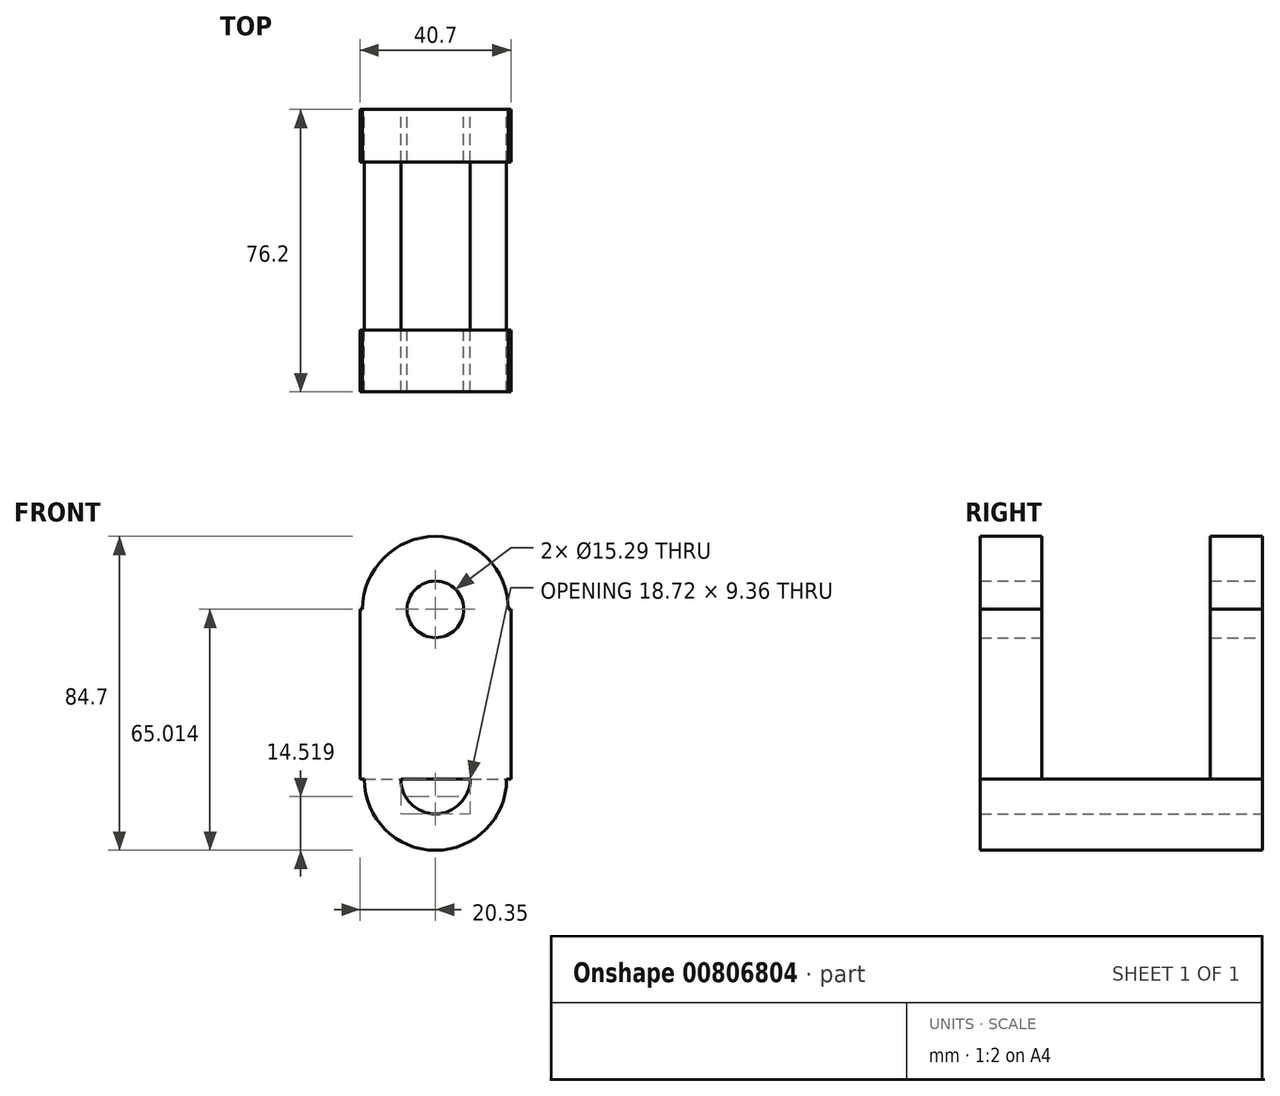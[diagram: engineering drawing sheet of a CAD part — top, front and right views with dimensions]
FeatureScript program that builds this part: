
annotation { "Feature Type Name" : "Feature", "Feature Type Description" : "" }
export const myFeature = defineFeature(function(context is Context, id is Id, definition is map)
    precondition{}
    {
        {
            var Q0;
            Q0=qCreatedBy(makeId("Front.planeOp"),FACE);
            var sketch = newSketch(context, id + "F0", { "sketchPlane" : qUnion([Q0])});
            skCircle(sketch, "E0", {"center": v(0, 0) * mm, "radius": 19.2 * mm});
            skCircle(sketch, "E1", {"center": v(0, 0) * mm, "radius": 9.36 * mm});
            skSolve(sketch);
        }
        {
            var Q0;
            Q0=makeQuery(id+"F0.imprint","IMPRINT",FACE,{"disambiguationData":[TD([[makeQuery(id+"F0.imprint","IMPRINT",EDGE,{"derivedFrom":sQuery(id+"F0.wireOp",EDGE,"E0")}),1.0]])]});
            extrude(context, id + "F1", {"entities" : qUnion([Q0]), "endBound" : BoundingType.SYMMETRIC, "depth" : 76.2 * mm, "offsetDistance" : 25.4 * mm});
        }
        {
            var Q0;
            Q0=qCreatedBy(makeId("Front.planeOp"),FACE);
            var sketch = newSketch(context, id + "F2", { "sketchPlane" : qUnion([Q0])});
            skLineSegment(sketch, "E2.bottom", {"start": v(-20.35, 0) * mm, "end": v(20.35, 0) * mm});
            skLineSegment(sketch, "E2.top", {"start": v(-20.35, 45.81) * mm, "end": v(-19.68, 45.81) * mm});
            skLineSegment(sketch, "E2.left", {"start": v(-20.35, 0) * mm, "end": v(-20.35, 45.81) * mm});
            skLineSegment(sketch, "E2.right", {"start": v(20.35, 0) * mm, "end": v(20.35, 45.81) * mm});
            skArc(sketch, "E3", {"start": v(19.68, 45.81) * mm, "mid": v(0, 65.5) * mm, "end": v(-19.68, 45.81) * mm});
            skLineSegment(sketch, "E4.trimOffspring", {"start": v(19.68, 45.81) * mm, "end": v(20.35, 45.81) * mm});
            skCircle(sketch, "E5", {"center": v(0, 45.81) * mm, "radius": 7.64 * mm});
            skSolve(sketch);
        }
        {
            var Q0;
            Q0=makeQuery(id+"F2.imprint","IMPRINT",FACE,{"disambiguationData":[TD([[makeQuery(id+"F2.imprint","IMPRINT",EDGE,{"derivedFrom":sQuery(id+"F2.wireOp",EDGE,"E2.bottom")}),1.0]])]});
            extrude(context, id + "F3", {"entities" : qUnion([Q0]), "operationType" : NewBodyOperationType.ADD, "endBound" : BoundingType.SYMMETRIC, "depth" : 76.2 * mm, "offsetDistance" : 25.4 * mm});
        }
        {
            var Q0;
            Q0=qCreatedBy(makeId("Right.planeOp"),FACE);
            var sketch = newSketch(context, id + "F4", { "sketchPlane" : qUnion([Q0])});
            skLineSegment(sketch, "E6.bottom", {"start": v(-21.46, 66.3) * mm, "end": v(23.95, 66.3) * mm});
            skLineSegment(sketch, "E6.top", {"start": v(-21.46, 0) * mm, "end": v(23.95, 0) * mm});
            skLineSegment(sketch, "E6.left", {"start": v(-21.46, 66.3) * mm, "end": v(-21.46, 0) * mm});
            skLineSegment(sketch, "E6.right", {"start": v(23.95, 66.3) * mm, "end": v(23.95, 0) * mm});
            skSolve(sketch);
        }
        {
            var Q0;
            Q0 = qSketchRegion(id + "F4", true);
            extrude(context, id + "F5", {"entities" : qUnion([Q0]), "operationType" : NewBodyOperationType.REMOVE, "endBound" : BoundingType.SYMMETRIC, "oppositeDirection" : true, "depth" : 228.6 * mm, "offsetDistance" : 25.4 * mm});
        }
    });
